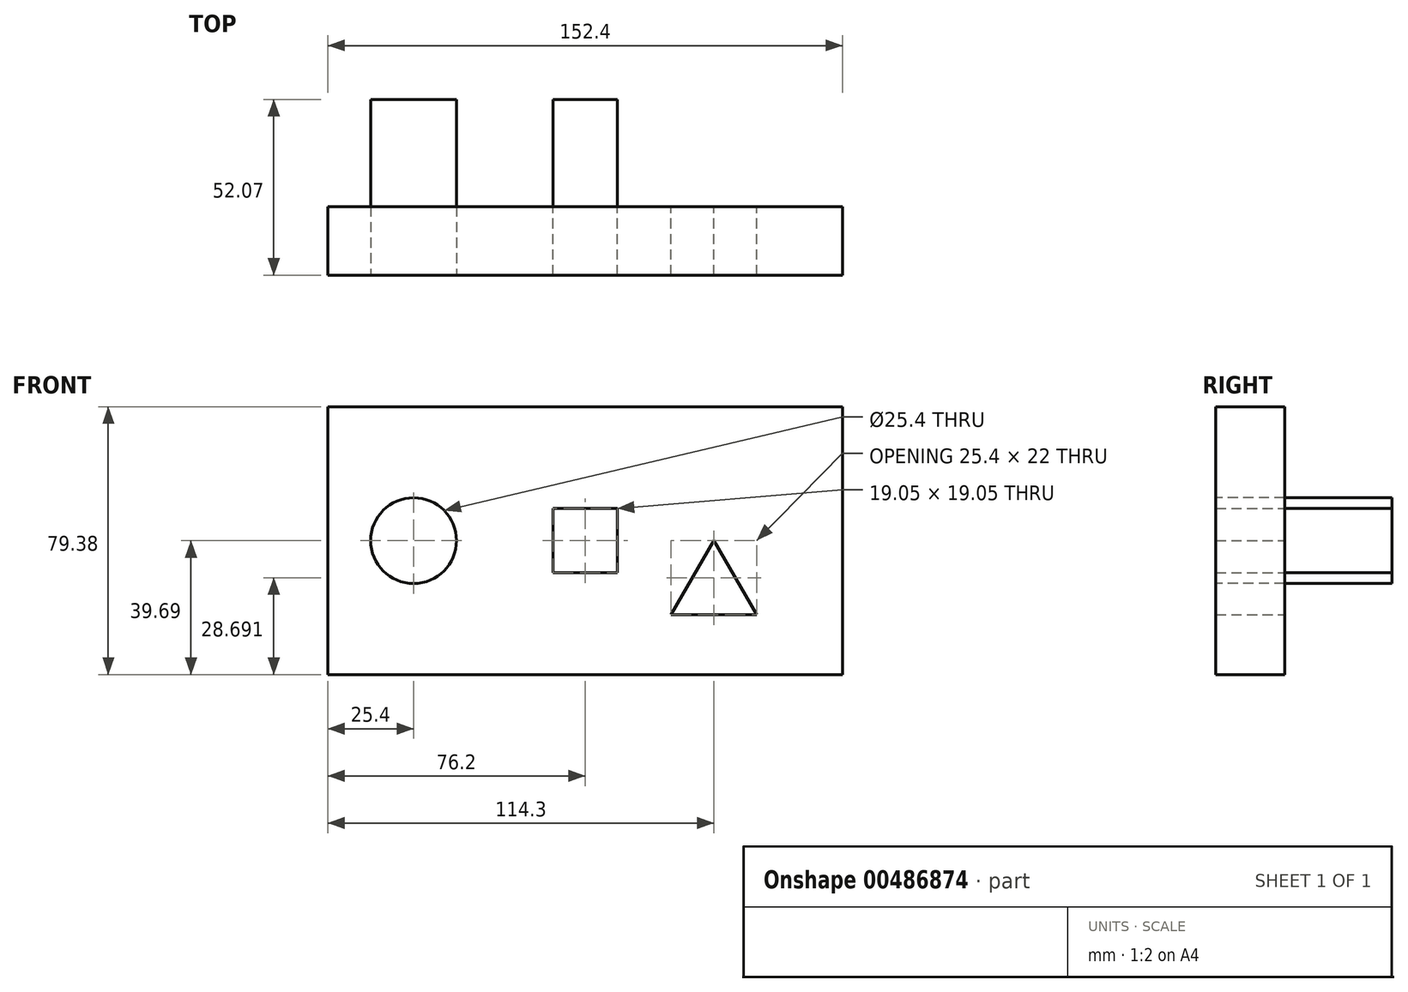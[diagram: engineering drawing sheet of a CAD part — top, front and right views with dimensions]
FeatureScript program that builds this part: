
annotation { "Feature Type Name" : "Feature", "Feature Type Description" : "" }
export const myFeature = defineFeature(function(context is Context, id is Id, definition is map)
    precondition{}
    {
        {
            var Q0;
            Q0=qCreatedBy(makeId("Front.planeOp"),FACE);
            var sketch = newSketch(context, id + "F0", { "sketchPlane" : qUnion([Q0])});
            skLineSegment(sketch, "E0", {"start": v(6.35, 0) * mm, "end": v(-6.35, -22) * mm});
            skLineSegment(sketch, "E1", {"start": v(-6.35, -22) * mm, "end": v(19.05, -22) * mm});
            skLineSegment(sketch, "E2", {"start": v(19.05, -22) * mm, "end": v(6.35, 0) * mm});
            skLineSegment(sketch, "E3.bottom", {"start": v(-22.22, 9.53) * mm, "end": v(-41.27, 9.53) * mm});
            skLineSegment(sketch, "E3.top", {"start": v(-22.23, -9.53) * mm, "end": v(-41.27, -9.53) * mm});
            skLineSegment(sketch, "E3.left", {"start": v(-22.22, 9.53) * mm, "end": v(-22.23, -9.53) * mm});
            skLineSegment(sketch, "E3.right", {"start": v(-41.27, 9.53) * mm, "end": v(-41.27, -9.52) * mm});
            skPoint(sketch, "E3.middle", {"position": v(-31.75, 0) * mm});
            skCircle(sketch, "E4", {"center": v(-82.55, 0) * mm, "radius": 12.7 * mm});
            skLineSegment(sketch, "E5.bottom", {"start": v(44.45, 39.69) * mm, "end": v(-107.95, 39.69) * mm});
            skLineSegment(sketch, "E5.top", {"start": v(44.45, -39.69) * mm, "end": v(-107.95, -39.69) * mm});
            skLineSegment(sketch, "E5.left", {"start": v(44.45, 39.69) * mm, "end": v(44.45, -39.69) * mm});
            skLineSegment(sketch, "E5.right", {"start": v(-107.95, 39.69) * mm, "end": v(-107.95, -39.69) * mm});
            skSolve(sketch);
        }
        {
            var Q0;
            Q0=makeQuery(id+"F0.imprint","IMPRINT",FACE,{"disambiguationData":[TD([[makeQuery(id+"F0.imprint","IMPRINT",EDGE,{"derivedFrom":sQuery(id+"F0.wireOp",EDGE,"E0")}),-1.0]])]});
            extrude(context, id + "F1", {"entities" : qUnion([Q0]), "depth" : 20.32 * mm});
        }
        {
            var Q0;
            Q0=makeQuery(id+"F0.imprint","IMPRINT",FACE,{"disambiguationData":[TD([[makeQuery(id+"F0.imprint","IMPRINT",EDGE,{"derivedFrom":sQuery(id+"F0.wireOp",EDGE,"E4")}),1.0]])]});
            extrude(context, id + "F2", {"entities" : qUnion([Q0]), "oppositeDirection" : true, "depth" : 31.75 * mm, "hasSecondDirection" : true, "secondDirectionOppositeDirection" : false, "secondDirectionDepth" : 20.32 * mm});
        }
        {
            var Q0;
            Q0=makeQuery(id+"F0.imprint","IMPRINT",FACE,{"disambiguationData":[TD([[makeQuery(id+"F0.imprint","IMPRINT",EDGE,{"derivedFrom":sQuery(id+"F0.wireOp",EDGE,"E3.bottom")}),1.0]])]});
            extrude(context, id + "F3", {"entities" : qUnion([Q0]), "oppositeDirection" : true, "depth" : 31.75 * mm});
        }
    });
